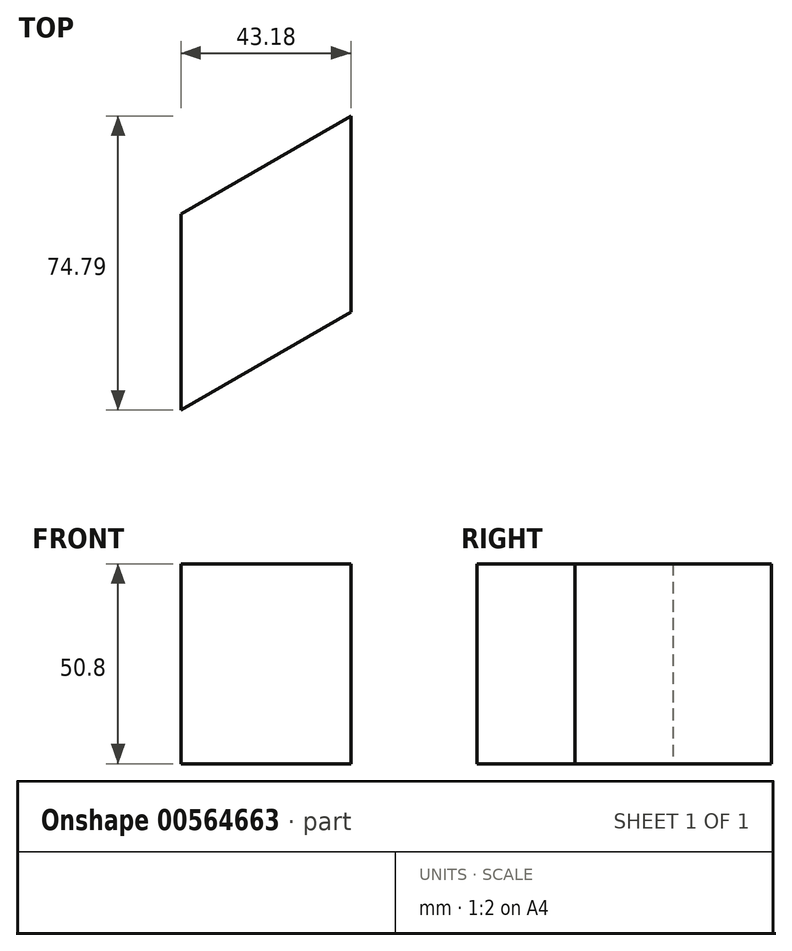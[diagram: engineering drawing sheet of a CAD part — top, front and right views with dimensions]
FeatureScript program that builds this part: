
annotation { "Feature Type Name" : "Feature", "Feature Type Description" : "" }
export const myFeature = defineFeature(function(context is Context, id is Id, definition is map)
    precondition{}
    {
        {
            var Q0;
            Q0=qCreatedBy(makeId("Top.planeOp"),FACE);
            var sketch = newSketch(context, id + "F0", { "sketchPlane" : qUnion([Q0])});
            skLineSegment(sketch, "E0", {"start": v(0, 0) * mm, "end": v(0, 49.86) * mm});
            skLineSegment(sketch, "E1", {"start": v(0, 49.86) * mm, "end": v(43.18, 74.79) * mm});
            skLineSegment(sketch, "E2", {"start": v(43.18, 74.79) * mm, "end": v(43.18, 24.93) * mm});
            skLineSegment(sketch, "E3", {"start": v(43.18, 24.93) * mm, "end": v(0, 0) * mm});
            skSolve(sketch);
        }
        {
            var Q0;
            Q0 = qSketchRegion(id + "F0", true);
            extrude(context, id + "F1", {"entities" : qUnion([Q0]), "depth" : 50.8 * mm, "offsetDistance" : 25.4 * mm});
        }
    });
